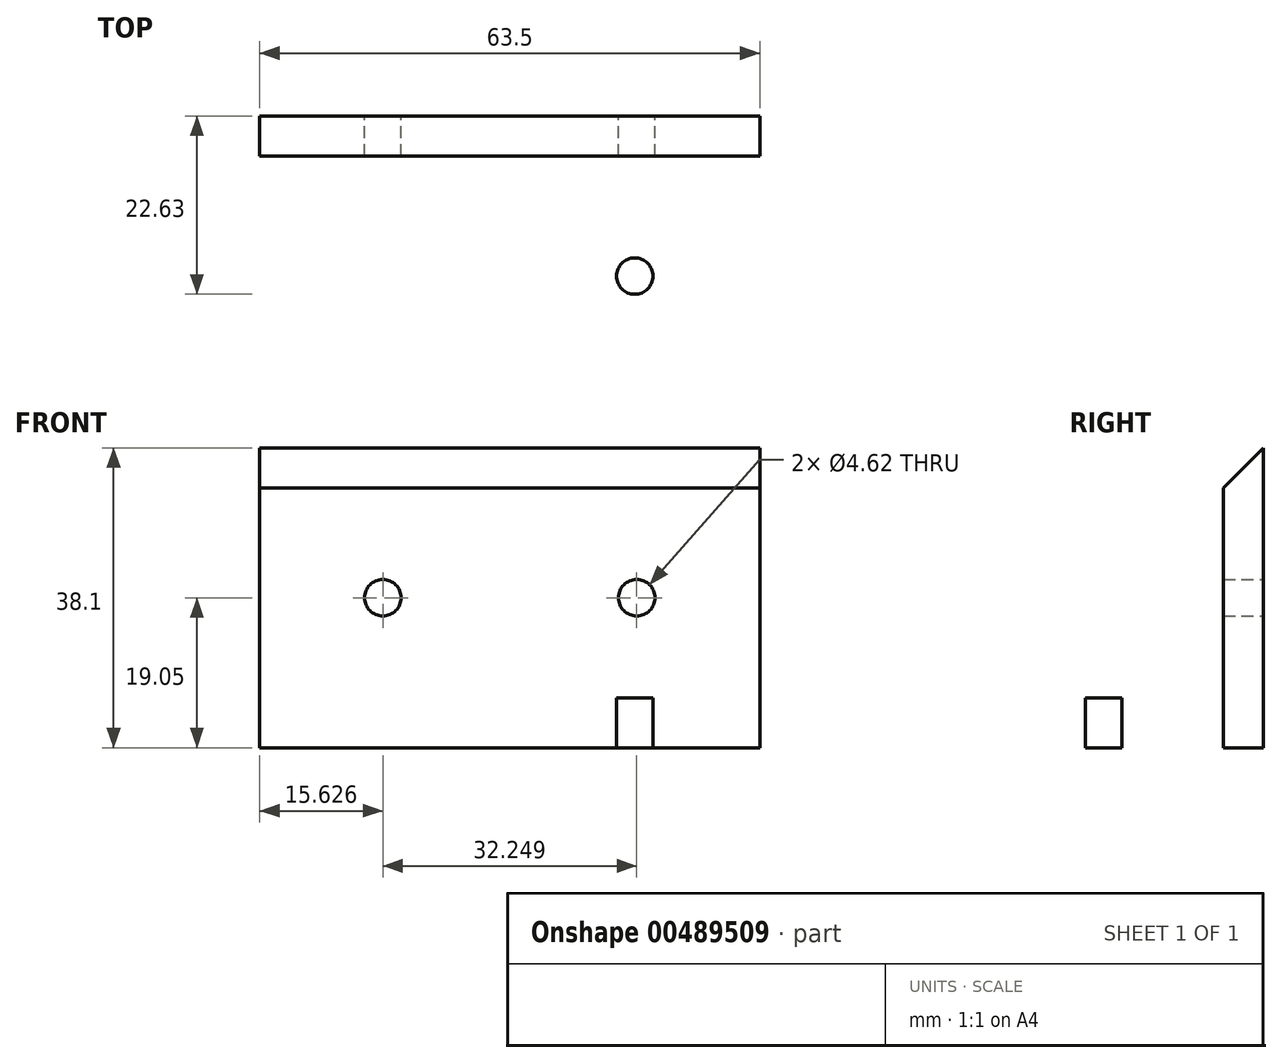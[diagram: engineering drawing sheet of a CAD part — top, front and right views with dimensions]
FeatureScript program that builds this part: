
annotation { "Feature Type Name" : "Feature", "Feature Type Description" : "" }
export const myFeature = defineFeature(function(context is Context, id is Id, definition is map)
    precondition{}
    {
        {
            var Q0;
            Q0=qCreatedBy(makeId("Front.planeOp"),FACE);
            var sketch = newSketch(context, id + "F0", { "sketchPlane" : qUnion([Q0])});
            skLineSegment(sketch, "E0.bottom", {"start": v(0, 0) * mm, "end": v(31.75, 0) * mm});
            skLineSegment(sketch, "E0.top", {"start": v(0, 38.1) * mm, "end": v(30.75, 38.1) * mm});
            skLineSegment(sketch, "E0.left", {"start": v(0, 0) * mm, "end": v(0, 38.1) * mm});
            skPoint(sketch, "E1.orphan", {"position": v(0, 19.05) * mm});
            skLineSegment(sketch, "E2", {"start": v(0, 19.05) * mm, "end": v(31.25, 19.05) * mm});
            skCircle(sketch, "E3", {"center": v(15.63, 19.05) * mm, "radius": 2.31 * mm});
            skLineSegment(sketch, "E4", {"start": v(31.75, 0) * mm, "end": v(31.75, 38.1) * mm});
            skLineSegment(sketch, "E5", {"start": v(30.75, 38.1) * mm, "end": v(31.75, 38.1) * mm});
            skLineSegment(sketch, "E6.MirrorCS", {"start": v(32.75, 38.1) * mm, "end": v(31.75, 38.1) * mm});
            skPoint(sketch, "E7.MirrorP", {"position": v(63.5, 19.05) * mm});
            skLineSegment(sketch, "E8.MirrorCS", {"start": v(63.5, 0) * mm, "end": v(31.75, 0) * mm});
            skLineSegment(sketch, "E9.MirrorCS", {"start": v(63.5, 38.1) * mm, "end": v(32.75, 38.1) * mm});
            skLineSegment(sketch, "E10.MirrorCS", {"start": v(63.5, 19.05) * mm, "end": v(32.25, 19.05) * mm});
            skLineSegment(sketch, "E11.MirrorCS", {"start": v(63.5, 0) * mm, "end": v(63.5, 38.1) * mm});
            skCircle(sketch, "E12.MirrorC", {"center": v(47.87, 19.05) * mm, "radius": 2.31 * mm});
            skSolve(sketch);
        }
        {
            var Q0;
            Q0 = qSketchRegion(id + "F0", true);
            extrude(context, id + "F1", {"entities" : qUnion([Q0]), "depth" : 5.08 * mm, "offsetDistance" : 25.4 * mm});
        }
        {
            var Q0;
            Q0=makeQuery(id+"F1.opExtrude","CAP_FACE",FACE,{"disambiguationData":[OSD([sQuery(id+"F0.wireOp",EDGE,"E0.bottom"),sQuery(id+"F0.wireOp",EDGE,"E0.top"),sQuery(id+"F0.wireOp",EDGE,"E0.left"),sQuery(id+"F0.wireOp",EDGE,"E3"),sQuery(id+"F0.wireOp",EDGE,"a26333b6-cbe1-480a-966c-ddbd438f7eba1.MirrorC"),sQuery(id+"F0.wireOp",EDGE,"a26333b6-cbe1-480a-966c-ddbd438f7eba2.MirrorCS"),sQuery(id+"F0.wireOp",EDGE,"49e4503b-9813-4501-a5fb-4088255afda90.MirrorCS"),sQuery(id+"F0.wireOp",EDGE,"09bf4277-9df5-4028-b87a-c8e9bbc99bcb0.MirrorCS")])],"isStart":false});
            var sketch = newSketch(context, id + "F2", { "sketchPlane" : qUnion([Q0])});
            skPoint(sketch, "E13", {"position": v(0, 0) * mm});
            skPoint(sketch, "E14", {"position": v(63.5, 0) * mm});
            skLineSegment(sketch, "E15.bottom", {"start": v(0, 0) * mm, "end": v(63.5, 0) * mm});
            skLineSegment(sketch, "E15.top", {"start": v(0, 6.35) * mm, "end": v(63.5, 6.35) * mm});
            skLineSegment(sketch, "E15.left", {"start": v(0, 0) * mm, "end": v(0, 6.35) * mm});
            skLineSegment(sketch, "E15.right", {"start": v(63.5, 0) * mm, "end": v(63.5, 6.35) * mm});
            skSolve(sketch);
        }
        {
            var Q0;
            Q0 = qSketchRegion(id + "F2", true);
            extrude(context, id + "F3", {"entities" : qUnion([Q0]), "operationType" : NewBodyOperationType.ADD, "depth" : 25.4 * mm, "offsetDistance" : 25.4 * mm});
        }
        {
            var Q0;
            Q0=makeQuery(id+"F3.opExtrude","SWEPT_FACE",FACE,{"disambiguationData":[OSD([sQuery(id+"F2.wireOp",EDGE,"E15.top")])]});
            var sketch = newSketch(context, id + "F4", { "sketchPlane" : qUnion([Q0])});
            skPoint(sketch, "E16", {"position": v(0, -17.78) * mm});
            skPoint(sketch, "E17", {"position": v(31.75, -30.48) * mm});
            skPoint(sketch, "E18", {"position": v(15.88, -20.32) * mm});
            skCircle(sketch, "E19", {"center": v(15.88, -20.32) * mm, "radius": 2.31 * mm});
            skPoint(sketch, "E20.MirrorP", {"position": v(47.62, -20.32) * mm});
            skCircle(sketch, "E21.MirrorC", {"center": v(47.62, -20.32) * mm, "radius": 2.31 * mm});
            skSolve(sketch);
        }
        {
            var Q0;
            Q0=makeQuery(id+"F4.imprint","IMPRINT",FACE,{"disambiguationData":[TD([[makeQuery(id+"F4.imprint","IMPRINT",EDGE,{"derivedFrom":sQuery(id+"F4.wireOp",EDGE,"E19")}),1.0]])]});
            var Q1;
            Q1=makeQuery(id+"F4.imprint","IMPRINT",FACE,{"disambiguationData":[TD([[makeQuery(id+"F4.imprint","IMPRINT",EDGE,{"derivedFrom":sQuery(id+"F4.wireOp",EDGE,"E21.MirrorC")}),-1.0]])]});
            extrude(context, id + "F5", {"entities" : qUnion([Q0, Q1]), "operationType" : NewBodyOperationType.REMOVE, "oppositeDirection" : true, "depth" : 25.4 * mm, "offsetDistance" : 25.4 * mm});
        }
        {
            var Q0;
            Q0=makeQuery(id+"F1.opExtrude","CAP_EDGE",EDGE,{"disambiguationData":[OSD([sQuery(id+"F0.wireOp",EDGE,"E0.top"),sQuery(id+"F0.wireOp",EDGE,"E5"),sQuery(id+"F0.wireOp",EDGE,"E6.MirrorCS"),sQuery(id+"F0.wireOp",EDGE,"E9.MirrorCS")])],"isStart":false});
            var Q1;
            Q1=makeQuery(id+"F3.opExtrude","CAP_EDGE",EDGE,{"disambiguationData":[OSD([sQuery(id+"F2.wireOp",EDGE,"E15.top")])],"isStart":false});
            var Q2;
            Q2=makeQuery(id+"F3.opExtrude","SWEPT_EDGE",EDGE,{"disambiguationData":[OSD([sQuery(id+"F0.wireOp",EDGE,"E0.left"),sQuery(id+"F2.wireOp",EDGE,"E15.top"),sQuery(id+"F2.wireOp",EDGE,"E15.left")])]});
            var Q3;
            Q3=makeQuery(id+"F3.opExtrude","SWEPT_EDGE",EDGE,{"disambiguationData":[OSD([sQuery(id+"F0.wireOp",EDGE,"E11.MirrorCS"),sQuery(id+"F2.wireOp",EDGE,"E15.top"),sQuery(id+"F2.wireOp",EDGE,"E15.right")])]});
            var Q4;
            Q4=makeQuery(id+"F1.opExtrude","CAP_EDGE",EDGE,{"disambiguationData":[OSD([sQuery(id+"F0.wireOp",EDGE,"E0.left")])],"isStart":false});
            var Q5;
            Q5=makeQuery(id+"F1.opExtrude","CAP_EDGE",EDGE,{"disambiguationData":[OSD([sQuery(id+"F0.wireOp",EDGE,"E11.MirrorCS")])],"isStart":false});
            chamfer(context, id + "F6", {"entities" : qUnion([Q0, Q1, Q2, Q3, Q4, Q5]), "width" : 5.08 * mm, "tangentPropagation" : true});
        }
    });
